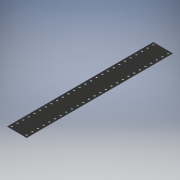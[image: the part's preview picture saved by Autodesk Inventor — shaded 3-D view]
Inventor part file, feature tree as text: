
AUTODESK INVENTOR PART (.ipt)
format: ipt  version: 2019 (Build 230136000, 136)  size: 172,032 bytes
history: native  units: mm
features: extrude x1, other x1
ambient origin geometry x8: Origin, YZ Plane, XZ Plane, XY Plane, X Axis, Y Axis, Z Axis, Center Point
bodies: Body1 (feature_tree)
feature tree (2):
  extrude  "Foam Body"  Depth=1419.0mm
  other  "Foam Scheme"
